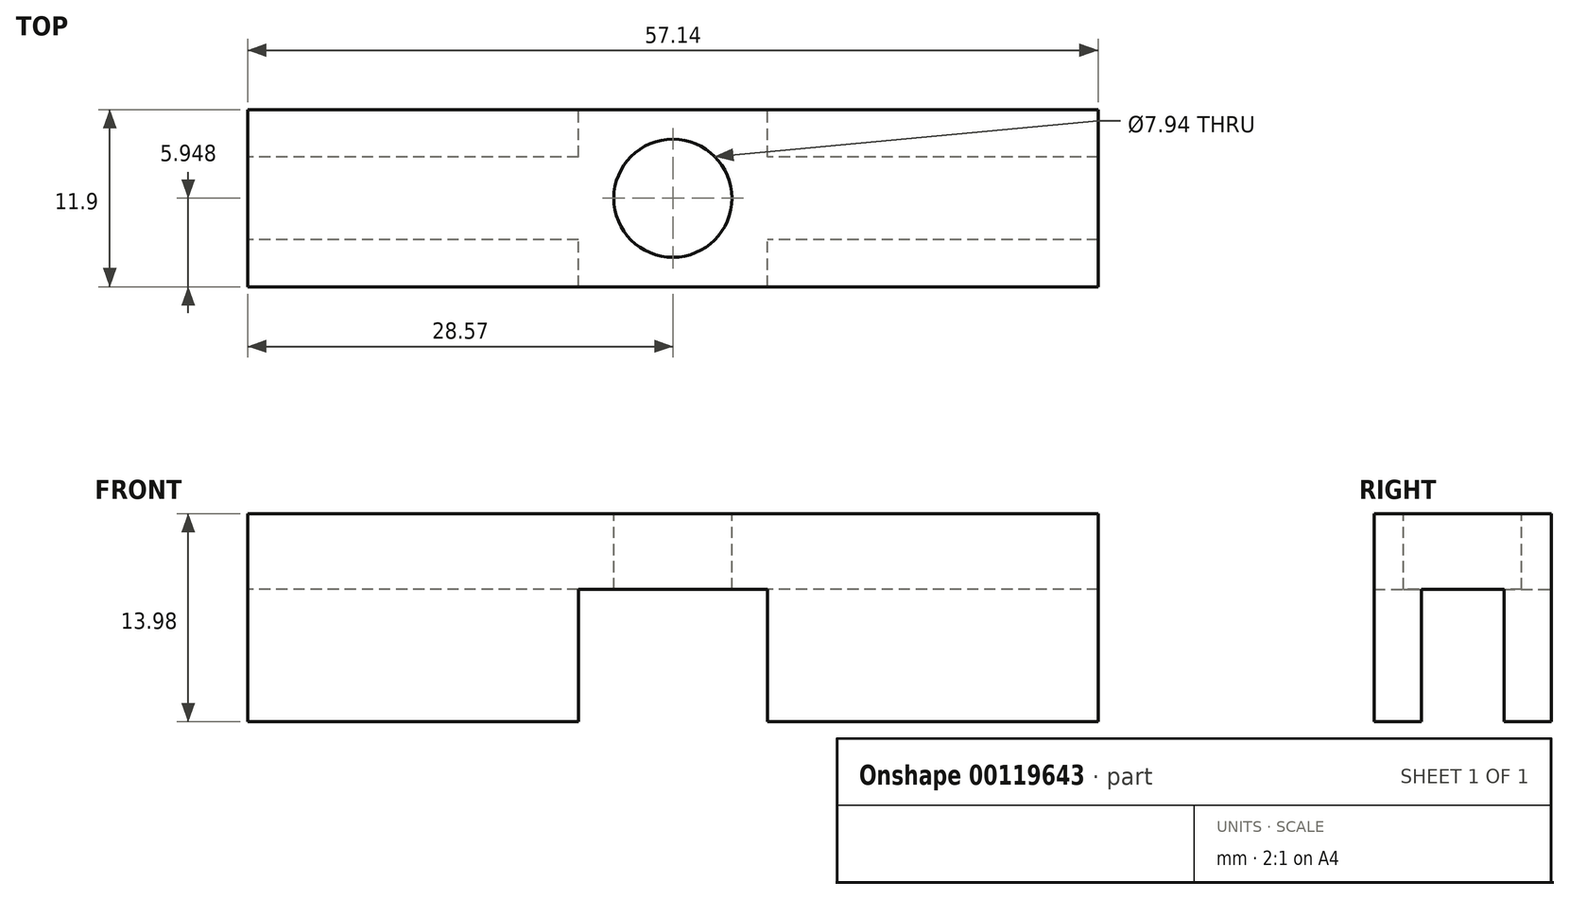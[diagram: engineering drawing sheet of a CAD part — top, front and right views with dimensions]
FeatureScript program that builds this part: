
annotation { "Feature Type Name" : "Feature", "Feature Type Description" : "" }
export const myFeature = defineFeature(function(context is Context, id is Id, definition is map)
    precondition{}
    {
        {
            var Q0;
            Q0=qCreatedBy(makeId("Front.planeOp"),FACE);
            var sketch = newSketch(context, id + "F0", { "sketchPlane" : qUnion([Q0])});
            skLineSegment(sketch, "E0.bottom", {"start": v(28.58, -6.99) * mm, "end": v(-28.58, -6.99) * mm});
            skLineSegment(sketch, "E0.top", {"start": v(28.58, 6.99) * mm, "end": v(-28.58, 6.99) * mm});
            skLineSegment(sketch, "E0.left", {"start": v(28.58, -6.99) * mm, "end": v(28.58, 6.99) * mm});
            skLineSegment(sketch, "E0.right", {"start": v(-28.58, -6.99) * mm, "end": v(-28.58, 6.99) * mm});
            skPoint(sketch, "E0.middle", {"position": v(0, 0) * mm});
            skSolve(sketch);
        }
        {
            var Q0;
            Q0 = qSketchRegion(id + "F0", true);
            extrude(context, id + "F1", {"entities" : qUnion([Q0]), "depth" : 3.17 * mm});
        }
        {
            var Q0;
            Q0=makeQuery(id+"F1.opExtrude","CAP_FACE",FACE,{"disambiguationData":[OSD([sQuery(id+"F0.wireOp",EDGE,"E0.bottom"),sQuery(id+"F0.wireOp",EDGE,"E0.top"),sQuery(id+"F0.wireOp",EDGE,"E0.left"),sQuery(id+"F0.wireOp",EDGE,"E0.right")])],"isStart":true});
            var sketch = newSketch(context, id + "F2", { "sketchPlane" : qUnion([Q0])});
            skLineSegment(sketch, "E1.bottom", {"start": v(-28.58, 6.99) * mm, "end": v(28.58, 6.99) * mm});
            skLineSegment(sketch, "E1.top", {"start": v(-28.58, 1.9) * mm, "end": v(28.58, 1.9) * mm});
            skLineSegment(sketch, "E1.left", {"start": v(-28.58, 6.99) * mm, "end": v(-28.58, 1.9) * mm});
            skLineSegment(sketch, "E1.right", {"start": v(28.58, 6.99) * mm, "end": v(28.58, 1.9) * mm});
            skSolve(sketch);
        }
        {
            var Q0;
            Q0 = qSketchRegion(id + "F2", true);
            extrude(context, id + "F3", {"entities" : qUnion([Q0]), "operationType" : NewBodyOperationType.ADD, "depth" : 2.78 * mm});
        }
        {
            var Q0;
            Q0=makeQuery(id+"F1.opExtrude","SWEPT_BODY",BODY,{"disambiguationData":[OSD([sQuery(id+"F0.wireOp",EDGE,"E0.bottom"),sQuery(id+"F0.wireOp",EDGE,"E0.top"),sQuery(id+"F0.wireOp",EDGE,"E0.left"),sQuery(id+"F0.wireOp",EDGE,"E0.right")])]});
            var Q1;
            Q1=makeQuery(id+"F3.opExtrude","CAP_FACE",FACE,{"disambiguationData":[OSD([sQuery(id+"F2.wireOp",EDGE,"E1.bottom"),sQuery(id+"F2.wireOp",EDGE,"E1.top"),sQuery(id+"F2.wireOp",EDGE,"E1.left"),sQuery(id+"F2.wireOp",EDGE,"E1.right")])],"isStart":false});
            mirror(context, id + "F4", {"operationType" : NewBodyOperationType.ADD, "entities" : qUnion([Q0]), "mirrorPlane" : qUnion([Q1])});
        }
        {
            var Q0;
            {var subQ0=makeQuery(id+"F3.boolean.opBoolean","MERGE",FACE,{"derivedFrom":[makeQuery(id+"F1.opExtrude","SWEPT_FACE",FACE,{"disambiguationData":[OSD([sQuery(id+"F0.wireOp",EDGE,"E0.top")])]}),makeQuery(id+"F3.opExtrude","SWEPT_FACE",FACE,{"disambiguationData":[OSD([sQuery(id+"F2.wireOp",EDGE,"E1.bottom")])]})]});Q0=makeQuery(id+"F4.boolean.opBoolean","MERGE",FACE,{"derivedFrom":[subQ0,makeQuery(id+"F4.opPattern","COPY",FACE,{"derivedFrom":subQ0,"instanceName":"1"})]});}
            var sketch = newSketch(context, id + "F5", { "sketchPlane" : qUnion([Q0])});
            skCircle(sketch, "E2", {"center": v(0, 2.78) * mm, "radius": 3.97 * mm});
            skPoint(sketch, "E2.centerSnap0", {"position": v(0, 8.73) * mm});
            skPoint(sketch, "E2.centerSnap1", {"position": v(28.58, 2.78) * mm});
            skSolve(sketch);
        }
        {
            var Q0;
            Q0 = qSketchRegion(id + "F5", true);
            extrude(context, id + "F6", {"entities" : qUnion([Q0]), "operationType" : NewBodyOperationType.REMOVE, "endBound" : BoundingType.THROUGH_ALL, "oppositeDirection" : true, "depth" : 25.4 * mm});
        }
        {
            var Q0;
            Q0=makeQuery(id+"F1.opExtrude","SWEPT_FACE",FACE,{"disambiguationData":[OSD([sQuery(id+"F0.wireOp",EDGE,"E0.bottom")])]});
            var sketch = newSketch(context, id + "F7", { "sketchPlane" : qUnion([Q0])});
            skLineSegment(sketch, "E3.bottom", {"start": v(6.35, 3.18) * mm, "end": v(-6.35, 3.18) * mm});
            skLineSegment(sketch, "E3.top", {"start": v(6.35, -8.73) * mm, "end": v(-6.35, -8.73) * mm});
            skLineSegment(sketch, "E3.left", {"start": v(6.35, 3.18) * mm, "end": v(6.35, -8.73) * mm});
            skLineSegment(sketch, "E3.right", {"start": v(-6.35, 3.18) * mm, "end": v(-6.35, -8.73) * mm});
            skPoint(sketch, "E3.middle", {"position": v(0, -2.78) * mm});
            skSolve(sketch);
        }
        {
            var Q0;
            Q0 = qSketchRegion(id + "F7", true);
            extrude(context, id + "F8", {"entities" : qUnion([Q0]), "operationType" : NewBodyOperationType.REMOVE, "oppositeDirection" : true, "depth" : 8.9 * mm});
        }
    });
